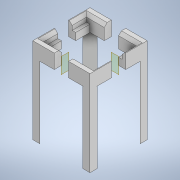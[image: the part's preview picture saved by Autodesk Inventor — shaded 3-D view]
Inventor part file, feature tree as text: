
AUTODESK INVENTOR PART (.ipt)
format: ipt  version: 2021 (Build 250183000, 183)  size: 157,696 bytes
history: native  units: mm
features: extrude x3, sketch x3, plane x2, mirror x2, other x1, chamfer x1
ambient origin geometry x8: Origin, YZ Plane, XZ Plane, XY Plane, X Axis, Y Axis, Z Axis, Center Point
bodies: Body1 (feature_tree)
feature tree (12):
  other  "Sólido1"
  extrude  "Extrusión1"  Depth=5.0mm
  extrude  "Extrusión2"  Depth=5.0mm
  extrude  "Extrusión3"  Depth=10.0mm TaperAngle=0.0deg
  chamfer  "Chaflán1"  Distance=2.5mm
  plane  "Plano de trabajo1"
  plane  "Plano de trabajo2"
  mirror  "Simetría1"
  mirror  "Simetría2"
  sketch  "Boceto1"  dims[d0=10.0mm d1=5.0mm]
  sketch  "Boceto2"  dims[d2=10.0mm d3=5.0mm]
  sketch  "Boceto3"  dims[d4=2.5mm d5=10.0mm d6=0.0mm d7=2.5mm d8=5.0mm d9=0.0mm d10=50.0mm d11=0.0mm d12=2.0mm d13=2.0mm d14=45.0deg d15=5.0mm d16=5.0mm]
